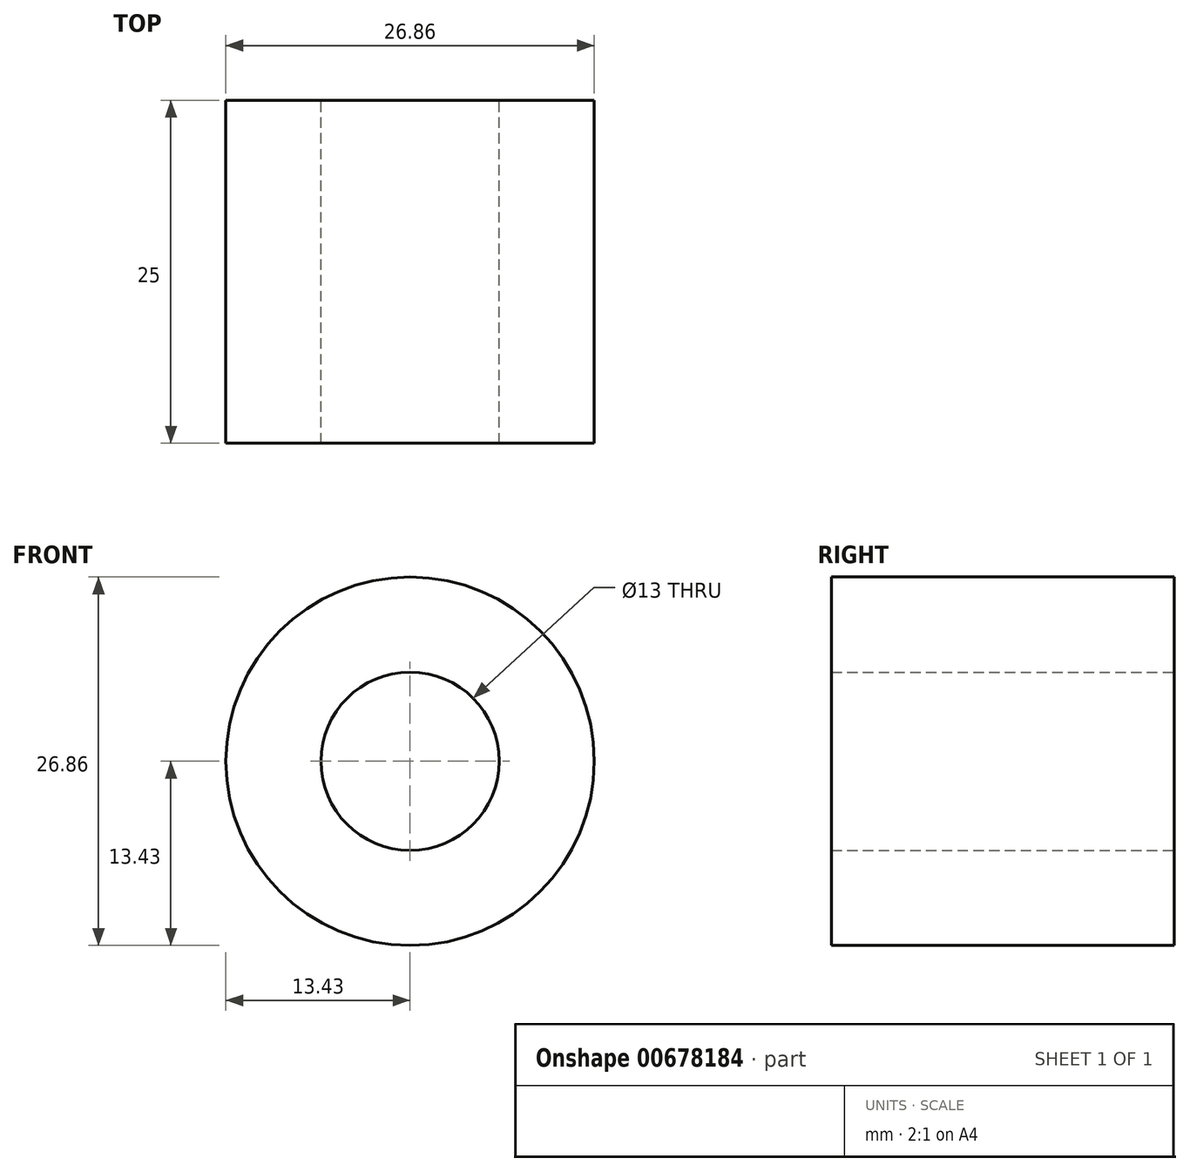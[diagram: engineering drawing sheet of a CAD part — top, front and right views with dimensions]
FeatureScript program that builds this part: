
annotation { "Feature Type Name" : "Feature", "Feature Type Description" : "" }
export const myFeature = defineFeature(function(context is Context, id is Id, definition is map)
    precondition{}
    {
        {
            var Q0;
            Q0=qCreatedBy(makeId("Front.planeOp"),FACE);
            var sketch = newSketch(context, id + "F0", { "sketchPlane" : qUnion([Q0])});
            skCircle(sketch, "E0", {"center": v(0, 0) * mm, "radius": 13.43 * mm});
            skCircle(sketch, "E1", {"center": v(0, 0) * mm, "radius": 14.67 * mm, "construction": true});
            skCircle(sketch, "E2", {"center": v(0, 0) * mm, "radius": 15.88 * mm, "construction": true});
            skLineSegment(sketch, "E3", {"start": v(0, 0) * mm, "end": v(0, 99.1) * mm, "construction": true});
            skLineSegment(sketch, "E4", {"start": v(0, 0) * mm, "end": v(-8, 122.09) * mm, "construction": true});
            skLineSegment(sketch, "E5", {"start": v(0, 14.67) * mm, "end": v(-120.67, 14.67) * mm, "construction": true});
            skLineSegment(sketch, "E6", {"start": v(0, 14.67) * mm, "end": v(-118.03, -28.29) * mm, "construction": true});
            skCircle(sketch, "E7", {"center": v(0, 0) * mm, "radius": 13.78 * mm, "construction": true});
            skCircle(sketch, "E8", {"center": v(0, 14.67) * mm, "radius": 14.6 * mm, "construction": true});
            skCircle(sketch, "E9", {"center": v(-13.72, 9.67) * mm, "radius": 14.6 * mm, "construction": true});
            skLineSegment(sketch, "E10", {"start": v(-2.04, 13.27) * mm, "end": v(-2.12, 13.26) * mm});
            skLineSegment(sketch, "E11", {"start": v(-2.12, 13.26) * mm, "end": v(-2.12, 13.26) * mm});
            skCircle(sketch, "E12", {"center": v(0, 0) * mm, "radius": 6.5 * mm});
            skArc(sketch, "E13.MirrorCS", {"start": v(-2.04, 13.27) * mm, "mid": v(-1.92, 17.87) * mm, "end": v(-0.32, 22.18) * mm});
            skArc(sketch, "E14.MirrorCS", {"start": v(2.04, 13.27) * mm, "mid": v(1.92, 17.87) * mm, "end": v(0.32, 22.18) * mm});
            skLineSegment(sketch, "E15", {"start": v(-0.32, 22.18) * mm, "end": v(0.32, 22.18) * mm});
            skSolve(sketch);
        }
        {
            var Q0;
            {var subQ0=sQuery(id+"F0.wireOp",EDGE,"E10");Q0=makeQuery(id+"F0.imprint","IMPRINT",FACE,{"disambiguationData":[TD([[makeQuery(id+"F0.imprint","IMPRINT",EDGE,{"derivedFrom":subQ0}),1.0]])]});}
            extrude(context, id + "F1", {"entities" : qUnion([Q0]), "depth" : 25 * mm, "offsetDistance" : 25 * mm});
        }
        {
            var Q0;
            Q0=makeQuery(id+"F1.opExtrude","SWEPT_BODY",BODY,{"disambiguationData":[OSD([sQuery(id+"F0.wireOp",EDGE,"E0"),sQuery(id+"F0.wireOp",EDGE,"NmizqAiV-zcEd-wW1i-qfzH-Hc12WR1YokAQ"),sQuery(id+"F0.wireOp",EDGE,"fbdf0611-0ef5-4687-8596-0c79478fe7200.MirrorCS"),sQuery(id+"F0.wireOp",EDGE,"E10"),sQuery(id+"F0.wireOp",EDGE,"pZYjaMaG-vTmR-xlgZ-VFzj-i6ecItI8BHiG")])]});
            var Q1;
            Q1=makeQuery(id+"F1.opExtrude","SWEPT_FACE",FACE,{"disambiguationData":[OSD([sQuery(id+"F0.wireOp",EDGE,"E0")])]});
            circularPattern(context, id + "F2", {"operationType" : NewBodyOperationType.ADD, "entities" : qUnion([Q0]), "axis" : qUnion([Q1]), "angle" : 360 * degree, "instanceCount" : 12, "equalSpace" : true});
        }
    });
